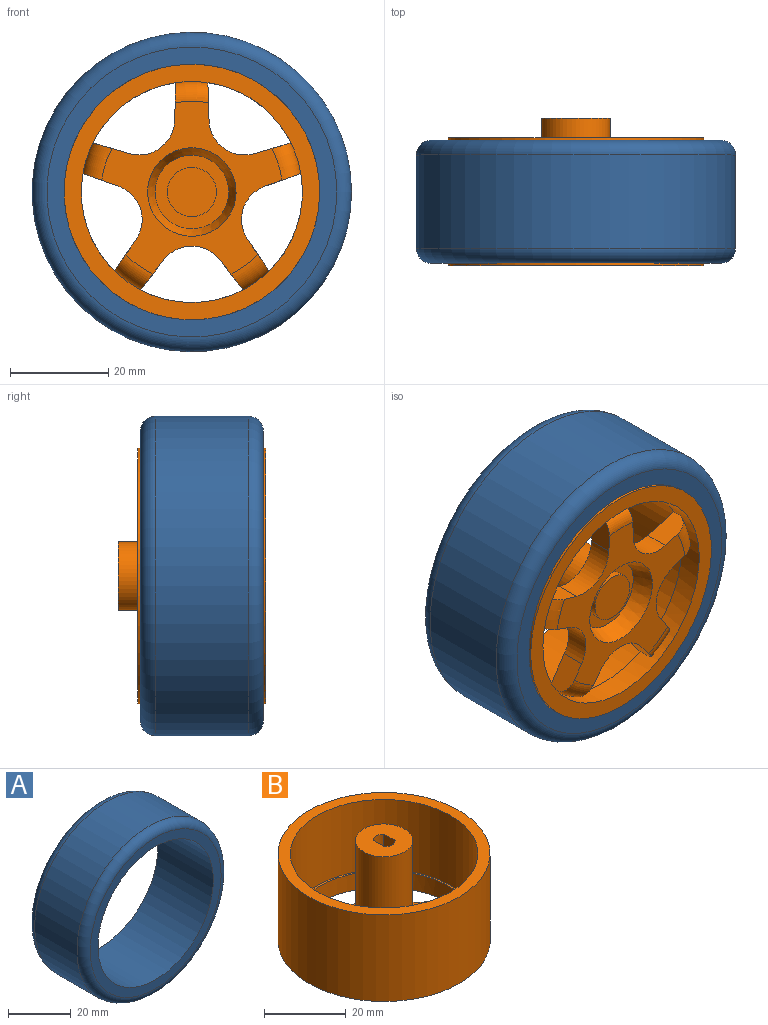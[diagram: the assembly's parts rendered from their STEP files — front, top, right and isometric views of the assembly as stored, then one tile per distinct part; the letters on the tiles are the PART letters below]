
ASSEMBLY  parts=2 mates=1
PART A: 6 faces, bbox 70.4x25x70.4 mm
  f0: torus R=29.5mm, axis (0,-1,0), area 930mm2, adj f3,f4
  f1: torus R=29.5mm, axis (0,-1,0), area 930mm2, adj f3,f5
  f2: cylinder r=26mm len=52mm, axis (0,1,0), area 4084.1mm2, adj f4,f5
  f3: cylinder r=32.5mm len=65mm, axis (0,1,0), area 3879.9mm2, adj f0,f1
  f4: plane 59x59mm, normal (0,-1,0), area 610.3mm2, adj f0,f2
  f5: plane 59x59mm, normal (0,1,0), area 610.3mm2, adj f1,f2
PART B: 38 faces, bbox 52x52x30 mm
  f0: cylinder r=2.7mm len=8mm, axis (0,0,1), area 33.2mm2, adj f33,f35,f36,f37
  f1: cylinder r=7mm len=25mm, axis (0,0,-1), area 1099.6mm2, adj f10,f33
  f2: torus R=18.5mm, axis (0,0,1), area 41.7mm2, adj f7,f12,f15,f18
  f3: cylinder r=5mm len=10mm, axis (0,0,1), area 47.1mm2, adj f27,f28
  f4: cone r=9mm half-angle=20.6deg, axis (0,0,-1), area 221.4mm2, adj f12,f27
  f5: cylinder r=7.2mm len=9.21mm, axis (0,0,-1), area 65.6mm2, adj f10,f12,f17,f18
  f6: cylinder r=7.2mm len=9.21mm, axis (0,0,-1), area 65.6mm2, adj f10,f12,f15,f16
  f7: cylinder r=22.5mm len=45mm, axis (0,0,-1), area 674.2mm2, adj f2,f10,f11,f13,f14,f15,f16,f17
  f8: cylinder r=23mm len=46mm, axis (0,0,1), area 3034.8mm2, adj f10,f23
  f9: cylinder r=26mm len=52mm, axis (0,0,-1), area 4247.4mm2, adj f11,f23
  f10: plane 46x46mm, normal (0,0,1), area 720.4mm2, adj f1,f5,f6,f7,f8,f13,f14,f15
  f11: plane 52x52mm, normal (0,0,-1), area 533.3mm2, adj f7,f9
  f12: plane 36.69x35.2mm, normal (0,0,-1), area 415mm2, adj f2,f4,f5,f6,f13,f14,f15,f16
  f13: plane 7.31x5mm, normal (-0.34,0.94,0), area 35.3mm2, adj f7,f10,f12,f24,f32
  f14: plane 6.42x5mm, normal (-0.83,-0.56,0), area 35.3mm2, adj f7,f10,f12,f24,f30
  f15: plane 7.76x5mm, normal (-1,-0.03,0), area 35.3mm2, adj f2,f6,f7,f10,f12
  f16: plane 7.46x5mm, normal (0.28,-0.96,0), area 35.3mm2, adj f6,f7,f10,f12,f32
  f17: plane 7.46x5mm, normal (-0.28,-0.96,0), area 35.3mm2, adj f5,f7,f10,f12,f31
  f18: plane 7.76x5mm, normal (1,-0.03,0), area 35.3mm2, adj f2,f5,f7,f10,f12
  f19: plane 6.42x5mm, normal (0.83,-0.56,0), area 35.3mm2, adj f7,f10,f12,f25,f29
  f20: plane 7.31x5mm, normal (0.34,0.94,0), area 35.3mm2, adj f7,f10,f12,f25,f31
  f21: plane 6.14x5mm, normal (0.79,0.61,0), area 35.3mm2, adj f7,f10,f12,f26,f30
  f22: plane 6.14x5mm, normal (-0.79,0.61,0), area 35.3mm2, adj f7,f10,f12,f26,f29
  f23: plane 52x52mm, normal (0,0,1), area 461.8mm2, adj f8,f9
  f24: cylinder r=7.2mm len=10.83mm, axis (0,0,-1), area 65.6mm2, adj f10,f12,f13,f14
  f25: cylinder r=7.2mm len=10.83mm, axis (0,0,-1), area 65.6mm2, adj f10,f12,f19,f20
  f26: cylinder r=7.2mm len=11.38mm, axis (0,0,-1), area 65.6mm2, adj f10,f12,f21,f22
  f27: plane 15x15mm, normal (0,0,-1), area 98.2mm2, adj f3,f4
  f28: plane 10x10mm, normal (0,0,-1), area 78.5mm2, adj f3
  f29: torus R=18.5mm, axis (0,0,1), area 41.7mm2, adj f7,f12,f19,f22
  f30: torus R=18.5mm, axis (0,0,1), area 41.7mm2, adj f7,f12,f14,f21
  f31: torus R=18.5mm, axis (0,0,1), area 41.7mm2, adj f7,f12,f17,f20
  f32: torus R=18.5mm, axis (0,0,1), area 41.7mm2, adj f7,f12,f13,f16
  f33: plane 14x14mm, normal (0,0,1), area 135.5mm2, adj f0,f1,f34,f35,f36
  f34: cylinder r=2.7mm len=8mm, axis (0,0,1), area 33.2mm2, adj f33,f35,f36,f37
  f35: plane 8x3.89mm, normal (-1,0,0), area 31.1mm2, adj f0,f33,f34,f37
  f36: plane 8x3.89mm, normal (1,0,0), area 31.1mm2, adj f0,f33,f34,f37
  f37: plane 5.4x3.75mm, normal (0,0,1), area 18.5mm2, adj f0,f34,f35,f36
PLACE A t=(151.93,-151.42,99.79)mm
PLACE B rot(axis=(-1,0,0),90deg) t=(151.93,-164.42,99.79)mm
MATE planar B.f0 <-> A.f0  axis (0,-1,0) through (151.93,-151.42,99.79)mm
